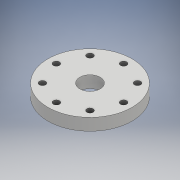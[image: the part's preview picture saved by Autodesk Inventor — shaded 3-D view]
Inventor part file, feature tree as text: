
AUTODESK INVENTOR PART (.ipt)
format: ipt  version: 2019 (Build 230136000, 136)  size: 123,904 bytes
history: native  units: mm
features: sketch x2, extrude x1, hole x1, thread x1, pattern_circular x1
ambient origin geometry x8: Origin, YZ Plane, XZ Plane, XY Plane, X Axis, Y Axis, Z Axis, Center Point
bodies: Solid1 (feature_tree)
feature tree (6):
  extrude  "Extrusion1"  Depth=70.0mm
  hole  "Hole1"  [1 undecoded]
  thread  "Thread1"  [1 undecoded]
  pattern_circular  "Circular Pattern1"  Count=8 Angle=360.0deg
  sketch  "Sketch1"  dims[d0=17.0mm d1=70.0mm]
  sketch  "Sketch2"  dims[d2=10.0mm d3=0.0mm d4=28.0mm d5=5.2mm d6=6.0mm d7=4.0mm d8=2.0mm d9=90.0deg d10=8.0mm d11=20.594885mm d12=10.0mm d13=0.0mm d14=80.0mm d15=360.0deg]
note: 2 required parameter values undecoded (feature->parameter linkage not recoverable at this tier; creation-order binding heuristic only, values carry confidence <= 0.55)
